# Revit family: Kitchen Stove Pertinger Ökoalpin 60BU
name_source: partatom
category: Generic Models
revit_build: Autodesk Revit 2016 (Build: 20150714_1515(x64)
units: mm (PartAtom-declared; Revit-internal decimal feet)

## family parameters
Always vertical = Yes
Can host rebar = No
Cut with Voids When Loaded = No
Part Type = Normal
Room Calculation Point = No
Round Connector Dimension = Use Diameter
Shared = No
Work Plane-Based = Yes

## types (1)
- Kitchen Stove Pertinger Ökoalpin 60BU
    Default Elevation = 0 mm  [stored 0 ft]
    Door Glass = M31.60 Lasilevyt, kirkas
    Door Material = M22.10 Terästuotteet, ruostumattomat
    Drawer Material = M22.10 Terästuotteet, ruostumattomat
    Frame Material = RAL Classic 9004, matta, ruisku
    Hob Material = M22.10 Terästuotteet, ruostumattomat
    Plinth Material = M22.10 Terästuotteet, ruostumattomat
    Width = 600 mm  [stored 1.9685 ft]

note: [stored X ft] marks values corroborated as IEEE doubles in the binary element streams (Revit-internal decimal feet)

## geometry (parser evidence)
native form markers: Blend x8, Sweep x7
no freeform markers — native parametric forms only
